# Revit family: Hager-FW-Hollow_wall-IP30-With_Cover-Without_DIN-Hosted-PL-pl
name_source: partatom
category: Electrical Equipment
units: mm (PartAtom-declared; Revit-internal decimal feet)

## family parameters
Cut with Voids When Loaded = No
Host = Face
Maintain Annotation Orientation = Yes
Panel Configuration = Two Columns, Circuits Across
Part Type = Panelboard
Room Calculation Point = No
Round Connector Dimension = Use Diameter
Shared = No

## types (1)
- FW-Hollow_wall_W853_H853_D125_12_Modular_Spacing-FWU53N
    BC_MODEL_ID = 1554255
    BC_OBJECT_ID = 513843
    BC_OBJECT_VERSION = #5
    BC_VARIANT_ID = 1178719
    Code hager = ADD-EC000214_EU
    Default Elevation = 0 mm  [stored 0 ft]
    EF000003 - Sposób montażu = Do ścian pustych
    EF000007 - Kolor = Biały
    EF000008 - Szerokość = 853 mm  [stored 2.79856 ft]
    EF000024 - Odporność na promieniowanie UV = No
    EF000040 - Wysokość = 853 mm  [stored 2.79856 ft]
    EF000049 - Głębokość = 125 mm  [stored 0.410105 ft]
    EF000116 - Numer RAL = 9010
    EF000118 - Z płytą montażową = No
    EF000218 - Głębokość wbudowania = 112 mm  [stored 0.367454 ft]
    EF000266 - Liczba rzędów = 5
    EF000332 - Wysokość wbudowania = 802 mm  [stored 2.63123 ft]
    EF000846 - Szerokość wbudowania = 810 mm
    EF001062 - Wykonanie zgodne z Dyrektywą Kompatybilności Elektromagnetycznej EMC = No
    EF001088 - Możliwość rozbudowy = Yes
    EF001131 - Głębokość wewnętrzna = 0 mm  [stored 0 ft]
    EF001134 - Szyna DIN = No
    EF002950 - Szerokość wyrażona liczbą modułów = 12
    EF004462 - Rodzaj zamknięcia = Inne
    EF005474 - Stopień ochrony (IP) = IP30
    EF006244 - Transparentna pokrywa/drzwi = No
    EF006306 - Z zamkiem = No
    EF009212 - Wykonanie/rodzaj pokrywy = Z otworem
    EF015776 - Listwa zaciskowa uziemienia = No
    EF015777 - Listwa zaciskowa przewodu neutralnego = No
    EF015941 - Drzwi przepuszczające sygnał = No
    ETIM class code = EC000214
    ETIM class name = Small distribution board
    HG000001-Number of columns-pl = 3
    HG000002-with door or cover-pl = Yes
    HG000003-Range-pl = FW
    HG000004-Manufacturer reference-pl = FWU53N
    HG000005-Thickness-pl = 2 mm  [stored 0.00656168 ft]
    HG000006-Flush mounted-pl = Yes
    HG000007-Number of empty columns-pl = 0
    HG000008-Number of empty rows-pl = 2
    HG000009-Double swing door-pl = Yes
    HG000010-Asymmetric doors-pl = Yes
    HG000011-Empty rows from bottom-pl = No
    HG000012-Door swing angle-pl = 90.00°
    HG000013-Door on the left-pl = No
    HG000014-Door on the right-pl = Yes
    HG000015-Clearance visibility-pl = Yes
    HG000016-Door 3D visibility-pl = Yes
    HG000017-Distance between poles-pl = 18 mm  [stored 0.0590551 ft]
    HG000060-RAL-number = 9010
    HG000099-Onfly Template ID-pl-PL = 507532
    HGEF000266-Liczba rzędów = 5
    HGEF0002950-Szerokość wyrażona liczbą modułów = 12
    Manufacturer = Hager
    Name = FW-Hollow_wall-IP30-With_Cover-Without_DIN-PL
    Name BIM&CO = Electricity
    Name hager = ADD_Enclosures_EC000214
    Reference = FW-Hollow_wall_W853_H853_D125_12_Modular_Spacing-FWU53N
    Uniformat = Low Tension Service & Dist.
    Uniformat code = D501001

note: [stored X ft] marks values corroborated as IEEE doubles in the binary element streams (Revit-internal decimal feet)

## geometry (parser evidence)
native form markers: Sweep x13
no freeform markers — native parametric forms only
